# Revit family: J2 PET Felt Blade Cloud Grid B
name_source: partatom
category: Specialty Equipment
units: mm (PartAtom-declared; Revit-internal decimal feet)

## family parameters
Always vertical = Yes
Cut with Voids When Loaded = No
Part Type = Normal
Room Calculation Point = No
Round Connector Dimension = Use Diameter
Shared = No
Work Plane-Based = No

## types (2) — shared parameters
Baffle Height (Max. 3'-11") = 0' - 7 3/4"
Default Elevation = 0' - 0"
Default End Spacing = 0' - 11 5/8"
Manufacturer = J2 Systems
Model = Blade Cloud Grid B
Product Line = Ceiling System
Release Date = 2019
Style Number = CSCGBL-B
URL = https://www.j2systems.net

## per-type parameters (varying)
| type | A Baffles in "X" direction | A Baffles in "Y" direction | B Baffles in "X" direction | B Baffles in "Y" direction | Nominal Length "X" (Max. 8') | Nominal Width "Y" (Max. 8') |
| Blade Cloud Grid B - 8'x8'x8" | 3 | 3 | 3 | 3 | 8' - 0" | 8' - 0" |
| Blade Cloud Grid B - 6'x6'x8" | 2 | 2 | 2 | 2 | 6' - 0" | 6' - 0" |

## geometry (parser evidence)
native form markers: Sweep x11
no freeform markers — native parametric forms only
